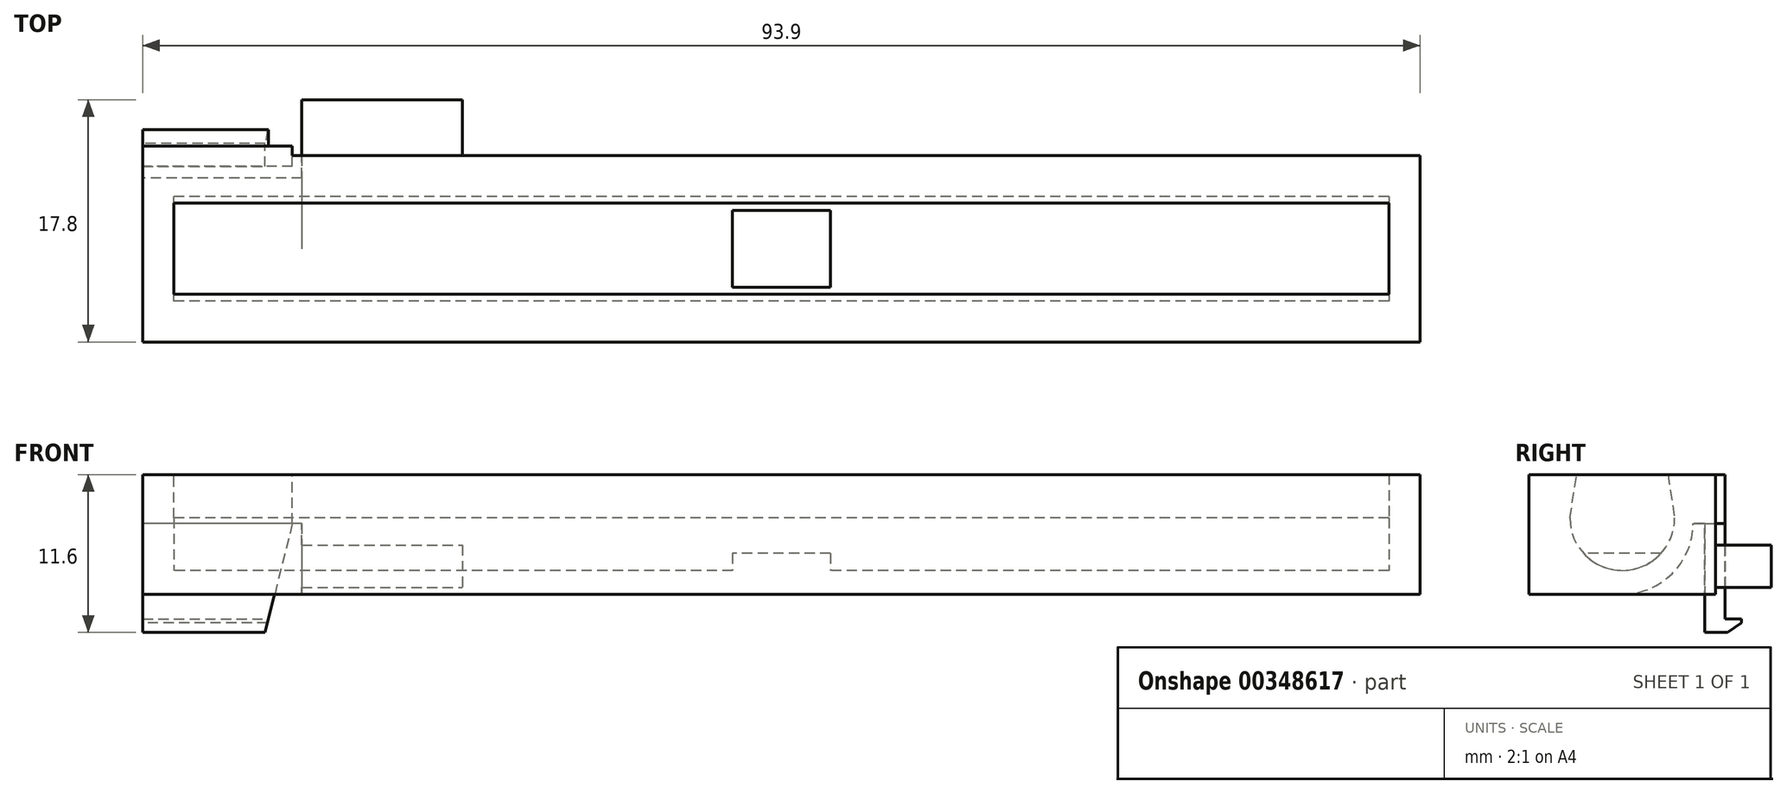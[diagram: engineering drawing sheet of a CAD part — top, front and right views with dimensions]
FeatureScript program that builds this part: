
annotation { "Feature Type Name" : "Feature", "Feature Type Description" : "" }
export const myFeature = defineFeature(function(context is Context, id is Id, definition is map)
    precondition{}
    {
        {
            var Q0;
            Q0=qCreatedBy(makeId("Top.planeOp"),FACE);
            var sketch = newSketch(context, id + "F0", { "sketchPlane" : qUnion([Q0])});
            skLineSegment(sketch, "E0.bottom", {"start": v(0, 0) * mm, "end": v(93.9, 0) * mm});
            skLineSegment(sketch, "E0.top", {"start": v(0, 13.7) * mm, "end": v(93.9, 13.7) * mm});
            skLineSegment(sketch, "E0.left", {"start": v(0, 0) * mm, "end": v(0, 13.7) * mm});
            skLineSegment(sketch, "E0.right", {"start": v(93.9, 0) * mm, "end": v(93.9, 13.7) * mm});
            skSolve(sketch);
        }
        {
            var Q0;
            Q0=makeQuery(id+"F0.imprint","IMPRINT",FACE,{"disambiguationData":[TD([[makeQuery(id+"F0.imprint","IMPRINT",EDGE,{"derivedFrom":sQuery(id+"F0.wireOp",EDGE,"E0.bottom")}),1.0]])]});
            extrude(context, id + "F1", {"entities" : qUnion([Q0]), "depth" : 8.8 * mm});
        }
        {
            var Q0;
            Q0=makeQuery(id+"F1.opExtrude","CAP_FACE",FACE,{"disambiguationData":[OSD([sQuery(id+"F0.wireOp",EDGE,"E0.bottom"),sQuery(id+"F0.wireOp",EDGE,"E0.top"),sQuery(id+"F0.wireOp",EDGE,"E0.left"),sQuery(id+"F0.wireOp",EDGE,"E0.right")])],"isStart":false});
            var sketch = newSketch(context, id + "F2", { "sketchPlane" : qUnion([Q0])});
            skLineSegment(sketch, "E1.bottom", {"start": v(2.3, 10.2) * mm, "end": v(91.6, 10.2) * mm});
            skLineSegment(sketch, "E1.top", {"start": v(2.3, 3.5) * mm, "end": v(91.6, 3.5) * mm});
            skLineSegment(sketch, "E1.left", {"start": v(2.3, 10.2) * mm, "end": v(2.3, 3.5) * mm});
            skLineSegment(sketch, "E1.right", {"start": v(91.6, 10.2) * mm, "end": v(91.6, 3.5) * mm});
            skSolve(sketch);
        }
        {
            var Q0;
            Q0=makeQuery(id+"F2.imprint","IMPRINT",FACE,{"disambiguationData":[TD([[makeQuery(id+"F2.imprint","IMPRINT",EDGE,{"derivedFrom":sQuery(id+"F2.wireOp",EDGE,"E1.bottom")}),-1.0]])]});
            extrude(context, id + "F3", {"entities" : qUnion([Q0]), "operationType" : NewBodyOperationType.REMOVE, "oppositeDirection" : true, "depth" : 7.8 * mm});
        }
        {
            var Q0;
            Q0=makeQuery(id+"F1.opExtrude","SWEPT_FACE",FACE,{"disambiguationData":[OSD([sQuery(id+"F0.wireOp",EDGE,"E0.top")])]});
            var sketch = newSketch(context, id + "F4", { "sketchPlane" : qUnion([Q0])});
            skLineSegment(sketch, "E2.bottom", {"start": v(-11.7, 3.6) * mm, "end": v(-23.5, 3.6) * mm});
            skLineSegment(sketch, "E2.top", {"start": v(-11.7, 0.5) * mm, "end": v(-23.5, 0.5) * mm});
            skLineSegment(sketch, "E2.left", {"start": v(-11.7, 3.6) * mm, "end": v(-11.7, 0.5) * mm});
            skLineSegment(sketch, "E2.right", {"start": v(-23.5, 3.6) * mm, "end": v(-23.5, 0.5) * mm});
            skSolve(sketch);
        }
        {
            var Q0;
            Q0=makeQuery(id+"F4.imprint","IMPRINT",FACE,{"disambiguationData":[TD([[makeQuery(id+"F4.imprint","IMPRINT",EDGE,{"derivedFrom":sQuery(id+"F4.wireOp",EDGE,"E2.bottom")}),1.0]])]});
            extrude(context, id + "F5", {"entities" : qUnion([Q0]), "operationType" : NewBodyOperationType.ADD, "depth" : 4.1 * mm});
        }
        {
            var Q0;
            Q0=makeQuery(id+"F1.opExtrude","SWEPT_FACE",FACE,{"disambiguationData":[OSD([sQuery(id+"F0.wireOp",EDGE,"E0.left")])]});
            var Q1;
            Q1=makeQuery(id+"F1.opExtrude","SWEPT_FACE",FACE,{"disambiguationData":[OSD([sQuery(id+"F0.wireOp",EDGE,"E0.right")])]});
            cPlane(context, id + "F6", {"entities" : qUnion([Q0, Q1]), "cplaneType" : CPlaneType.MID_PLANE, "offset" : 25 * mm, "width" : 150 * mm, "height" : 150 * mm});
        }
        {
            var Q0;
            Q0=makeQuery(id+"F1.opExtrude","SWEPT_FACE",FACE,{"disambiguationData":[OSD([sQuery(id+"F0.wireOp",EDGE,"E0.top")])]});
            var Q1;
            Q1=makeQuery(id+"F1.opExtrude","SWEPT_FACE",FACE,{"disambiguationData":[OSD([sQuery(id+"F0.wireOp",EDGE,"E0.bottom")])]});
            cPlane(context, id + "F7", {"entities" : qUnion([Q0, Q1]), "cplaneType" : CPlaneType.MID_PLANE, "offset" : 25 * mm, "width" : 150 * mm, "height" : 150 * mm});
        }
        {
            var Q0;
            Q0=makeQuery(id+"F3.boolean.opBoolean","COPY",FACE,{"derivedFrom":makeQuery(id+"F3.opExtrude","SWEPT_FACE",FACE,{"disambiguationData":[OSD([sQuery(id+"F2.wireOp",EDGE,"E1.left")])]})});
            var sketch = newSketch(context, id + "F8", { "sketchPlane" : qUnion([Q0])});
            skArc(sketch, "E3", {"start": v(3, 5.6) * mm, "mid": v(6.85, 1.76) * mm, "end": v(10.7, 5.6) * mm});
            skLineSegment(sketch, "E4", {"start": v(3, 5.6) * mm, "end": v(3.5, 8.8) * mm});
            skLineSegment(sketch, "E5", {"start": v(3.5, 8.8) * mm, "end": v(10.2, 8.8) * mm});
            skLineSegment(sketch, "E6", {"start": v(10.2, 8.8) * mm, "end": v(10.7, 5.6) * mm});
            skSolve(sketch);
        }
        {
            var Q0;
            Q0=makeQuery(id+"F3.boolean.opBoolean","COPY",EDGE,{"derivedFrom":makeQuery(id+"F3.opExtrude","CAP_EDGE",EDGE,{"disambiguationData":[OSD([sQuery(id+"F2.wireOp",EDGE,"E1.bottom")])],"isStart":false})});
            var Q1;
            Q1=makeQuery(id+"F3.boolean.opBoolean","COPY",EDGE,{"derivedFrom":makeQuery(id+"F3.opExtrude","CAP_EDGE",EDGE,{"disambiguationData":[OSD([sQuery(id+"F2.wireOp",EDGE,"E1.top")])],"isStart":false})});
            fillet(context, id + "F9", {"entities" : qUnion([Q0, Q1]), "radius" : 6.5 * mm, "tangentPropagation" : true, "allowEdgeOverflow" : false});
        }
        {
            var Q0;
            Q0 = qSketchRegion(id + "F8", true);
            var Q1;
            Q1=makeQuery(id+"F3.boolean.opBoolean","COPY",FACE,{"derivedFrom":makeQuery(id+"F3.opExtrude","SWEPT_FACE",FACE,{"disambiguationData":[OSD([sQuery(id+"F2.wireOp",EDGE,"E1.right")])]})});
            extrude(context, id + "F10", {"entities" : qUnion([Q0]), "operationType" : NewBodyOperationType.REMOVE, "endBound" : BoundingType.UP_TO_SURFACE, "endBoundEntityFace" : qUnion([Q1]), "depth" : 25 * mm});
        }
        {
            var Q0;
            Q0=qCreatedBy(makeId("Top.planeOp"),FACE);
            var sketch = newSketch(context, id + "F11", { "sketchPlane" : qUnion([Q0])});
            skLineSegment(sketch, "E7.bottom", {"start": v(43.35, 10.2) * mm, "end": v(50.55, 10.2) * mm});
            skLineSegment(sketch, "E7.top", {"start": v(43.35, 3.5) * mm, "end": v(50.55, 3.5) * mm});
            skLineSegment(sketch, "E7.left", {"start": v(43.35, 10.2) * mm, "end": v(43.35, 3.5) * mm});
            skLineSegment(sketch, "E7.right", {"start": v(50.55, 10.2) * mm, "end": v(50.55, 3.5) * mm});
            skSolve(sketch);
        }
        {
            var Q0;
            Q0 = qSketchRegion(id + "F11", true);
            extrude(context, id + "F12", {"entities" : qUnion([Q0]), "operationType" : NewBodyOperationType.ADD, "depth" : 3 * mm});
        }
        {
            var Q0;
            Q0=makeQuery(id+"F1.opExtrude","SWEPT_FACE",FACE,{"disambiguationData":[OSD([sQuery(id+"F0.wireOp",EDGE,"E0.left")])]});
            var sketch = newSketch(context, id + "F13", { "sketchPlane" : qUnion([Q0])});
            skArc(sketch, "E8", {"start": v(-12.05, 5.2) * mm, "mid": v(-6.85, 0) * mm, "end": v(-1.65, 5.2) * mm});
            skLineSegment(sketch, "E9", {"start": v(-13.7, 5.2) * mm, "end": v(-12.05, 5.2) * mm});
            skLineSegment(sketch, "E10", {"start": v(0, 5.2) * mm, "end": v(0, 0) * mm});
            skLineSegment(sketch, "E11", {"start": v(-6.85, 0) * mm, "end": v(-13.7, 0) * mm});
            skLineSegment(sketch, "E12", {"start": v(-13.7, 0) * mm, "end": v(-13.7, 5.2) * mm});
            skLineSegment(sketch, "E13.trimOffspring", {"start": v(-1.65, 5.2) * mm, "end": v(0, 5.2) * mm});
            skLineSegment(sketch, "E14", {"start": v(-6.85, 0) * mm, "end": v(0, 0) * mm});
            skSolve(sketch);
        }
        {
            var Q0;
            {var subQ0=sQuery(id+"F13.wireOp",EDGE,"E9");Q0=makeQuery(id+"F13.imprint","IMPRINT",FACE,{"disambiguationData":[TD([[makeQuery(id+"F13.imprint","IMPRINT",EDGE,{"derivedFrom":subQ0}),-1.0]])]});}
            var Q1;
            Q1=makeQuery(id+"F5.opExtrude","SWEPT_FACE",FACE,{"disambiguationData":[OSD([sQuery(id+"F4.wireOp",EDGE,"E2.left")])]});
            extrude(context, id + "F14", {"entities" : qUnion([Q0]), "operationType" : NewBodyOperationType.REMOVE, "endBound" : BoundingType.UP_TO_SURFACE, "oppositeDirection" : true, "endBoundEntityFace" : qUnion([Q1]), "depth" : 25 * mm});
        }
        {
            var Q0;
            Q0=makeQuery(id+"F14.boolean.opBoolean","COPY",FACE,{"derivedFrom":makeQuery(id+"F14.opExtrude","SWEPT_FACE",FACE,{"disambiguationData":[OSD([sQuery(id+"F13.wireOp",EDGE,"E9")])]})});
            var sketch = newSketch(context, id + "F15", { "sketchPlane" : qUnion([Q0])});
            skLineSegment(sketch, "E15.bottom", {"start": v(0, -14.4) * mm, "end": v(11, -14.4) * mm});
            skLineSegment(sketch, "E15.top", {"start": v(0, -12.9) * mm, "end": v(11, -12.9) * mm});
            skLineSegment(sketch, "E15.left", {"start": v(0, -14.4) * mm, "end": v(0, -12.9) * mm});
            skLineSegment(sketch, "E15.right", {"start": v(11, -14.4) * mm, "end": v(11, -12.9) * mm});
            skSolve(sketch);
        }
        {
            var Q0;
            Q0 = qSketchRegion(id + "F15", true);
            var Q1;
            Q1=makeQuery(id+"F1.opExtrude","CAP_FACE",FACE,{"disambiguationData":[OSD([sQuery(id+"F0.wireOp",EDGE,"E0.bottom"),sQuery(id+"F0.wireOp",EDGE,"E0.top"),sQuery(id+"F0.wireOp",EDGE,"E0.left"),sQuery(id+"F0.wireOp",EDGE,"E0.right")])],"isStart":false});
            extrude(context, id + "F16", {"entities" : qUnion([Q0]), "operationType" : NewBodyOperationType.ADD, "depth" : 8 * mm, "hasSecondDirection" : true, "secondDirectionBound" : SecondDirectionBoundingType.UP_TO_SURFACE, "secondDirectionOppositeDirection" : true, "secondDirectionBoundEntityFace" : qUnion([Q1]), "secondDirectionDepth" : 25 * mm});
        }
        {
            var Q0;
            Q0=makeQuery(id+"F16.opExtrude","SWEPT_FACE",FACE,{"disambiguationData":[OSD([sQuery(id+"F15.wireOp",EDGE,"E15.bottom")])]});
            var sketch = newSketch(context, id + "F17", { "sketchPlane" : qUnion([Q0])});
            skLineSegment(sketch, "E16", {"start": v(-11, 5.2) * mm, "end": v(-9, -2.8) * mm});
            skLineSegment(sketch, "E17", {"start": v(-9, -2.8) * mm, "end": v(-11, -2.8) * mm});
            skLineSegment(sketch, "E18", {"start": v(-11, -2.8) * mm, "end": v(-11, 5.2) * mm});
            skSolve(sketch);
        }
        {
            var Q0;
            Q0=makeQuery(id+"F17.imprint","IMPRINT",FACE,{"disambiguationData":[TD([[makeQuery(id+"F17.imprint","IMPRINT",EDGE,{"derivedFrom":sQuery(id+"F17.wireOp",EDGE,"E16")}),-1.0]])]});
            var Q1;
            Q1=makeQuery(id+"F16.opExtrude","SWEPT_FACE",FACE,{"disambiguationData":[OSD([sQuery(id+"F15.wireOp",EDGE,"E15.top")])]});
            extrude(context, id + "F18", {"entities" : qUnion([Q0]), "operationType" : NewBodyOperationType.REMOVE, "endBound" : BoundingType.UP_TO_SURFACE, "oppositeDirection" : true, "endBoundEntityFace" : qUnion([Q1]), "depth" : 25 * mm});
        }
        {
            var Q0;
            Q0=makeQuery(id+"F16.opExtrude","SWEPT_FACE",FACE,{"disambiguationData":[OSD([sQuery(id+"F15.wireOp",EDGE,"E15.bottom")])]});
            var sketch = newSketch(context, id + "F19", { "sketchPlane" : qUnion([Q0])});
            skLineSegment(sketch, "E19", {"start": v(-9, -2.8) * mm, "end": v(0, -2.8) * mm});
            skLineSegment(sketch, "E20", {"start": v(0, -1.8) * mm, "end": v(-9.25, -1.8) * mm});
            skLineSegment(sketch, "E21", {"start": v(0, -1.8) * mm, "end": v(0, -2.8) * mm});
            skLineSegment(sketch, "E22", {"start": v(-9.25, -1.8) * mm, "end": v(-9, -2.8) * mm});
            skSolve(sketch);
        }
        {
            var Q0;
            Q0=makeQuery(id+"F19.imprint","IMPRINT",FACE,{"disambiguationData":[TD([[makeQuery(id+"F19.imprint","IMPRINT",EDGE,{"derivedFrom":sQuery(id+"F19.wireOp",EDGE,"E19")}),-1.0]])]});
            extrude(context, id + "F20", {"entities" : qUnion([Q0]), "operationType" : NewBodyOperationType.ADD, "depth" : 1.2 * mm});
        }
        {
            var Q0;
            Q0=makeQuery(id+"F20.boolean.opBoolean","MERGE",FACE,{"derivedFrom":[makeQuery(id+"F16.boolean.opBoolean","MERGE",FACE,{"derivedFrom":[makeQuery(id+"F1.opExtrude","SWEPT_FACE",FACE,{"disambiguationData":[OSD([sQuery(id+"F0.wireOp",EDGE,"E0.left")])]}),makeQuery(id+"F16.opExtrude","SWEPT_FACE",FACE,{"disambiguationData":[OSD([sQuery(id+"F15.wireOp",EDGE,"E15.left")])]})]}),makeQuery(id+"F20.opExtrude","SWEPT_FACE",FACE,{"disambiguationData":[OSD([sQuery(id+"F19.wireOp",EDGE,"E21")])]})]});
            var sketch = newSketch(context, id + "F21", { "sketchPlane" : qUnion([Q0])});
            skLineSegment(sketch, "E23", {"start": v(-15.6, -2.1) * mm, "end": v(-14.6, -2.8) * mm});
            skLineSegment(sketch, "E24", {"start": v(-14.6, -2.8) * mm, "end": v(-15.6, -2.8) * mm});
            skLineSegment(sketch, "E25", {"start": v(-15.6, -2.8) * mm, "end": v(-15.6, -2.1) * mm});
            skSolve(sketch);
        }
        {
            var Q0;
            Q0=makeQuery(id+"F21.imprint","IMPRINT",FACE,{"disambiguationData":[TD([[makeQuery(id+"F21.imprint","IMPRINT",EDGE,{"derivedFrom":sQuery(id+"F21.wireOp",EDGE,"E23")}),-1.0]])]});
            extrude(context, id + "F22", {"entities" : qUnion([Q0]), "operationType" : NewBodyOperationType.REMOVE, "endBound" : BoundingType.UP_TO_NEXT, "oppositeDirection" : true, "depth" : 25 * mm});
        }
    });
